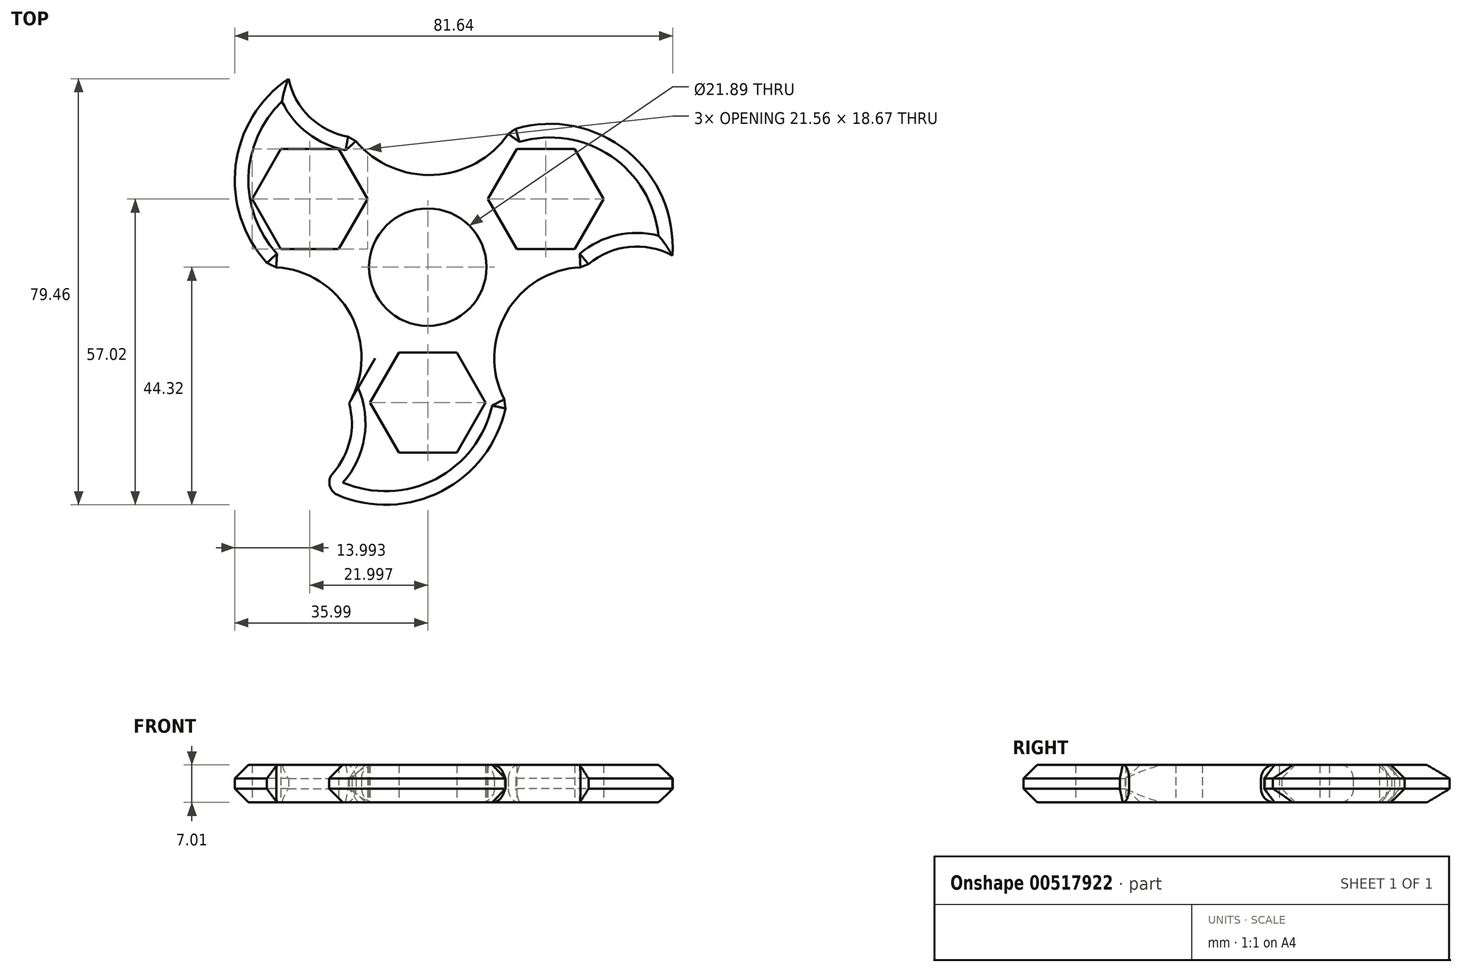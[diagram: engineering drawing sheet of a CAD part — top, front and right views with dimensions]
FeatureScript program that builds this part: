
annotation { "Feature Type Name" : "Feature", "Feature Type Description" : "" }
export const myFeature = defineFeature(function(context is Context, id is Id, definition is map)
    precondition{}
    {
        {
            var Q0;
            Q0=qCreatedBy(makeId("Top.planeOp"),FACE);
            var sketch = newSketch(context, id + "F0", { "sketchPlane" : qUnion([Q0])});
            skCircle(sketch, "E0.cCircle", {"center": v(0, 0) * mm, "radius": 12.7 * mm, "construction": true});
            skLineSegment(sketch, "E0.0", {"start": v(7.33, -12.7) * mm, "end": v(-7.33, -12.7) * mm});
            skLineSegment(sketch, "E0.1", {"start": v(-7.33, -12.7) * mm, "end": v(-14.66, 0) * mm});
            skLineSegment(sketch, "E0.2", {"start": v(-14.66, 0) * mm, "end": v(-7.33, 12.7) * mm});
            skLineSegment(sketch, "E0.4", {"start": v(7.33, 12.7) * mm, "end": v(14.66, 0) * mm});
            skLineSegment(sketch, "E0.5", {"start": v(14.66, 0) * mm, "end": v(7.33, -12.7) * mm});
            skCircle(sketch, "E1", {"center": v(0, 0) * mm, "radius": 10.95 * mm});
            skLineSegment(sketch, "E2.bottom", {"start": v(4.8, -12.7) * mm, "end": v(-4.8, -12.7) * mm});
            skLineSegment(sketch, "E3.MirrorCS", {"start": v(4.8, -76.2) * mm, "end": v(-4.8, -76.2) * mm});
            skLineSegment(sketch, "E4.MirrorCS", {"start": v(4.8, -73.66) * mm, "end": v(4.8, -76.2) * mm});
            skLineSegment(sketch, "E5.MirrorCS", {"start": v(14.66, -25.4) * mm, "end": v(7.33, -12.7) * mm});
            skLineSegment(sketch, "E6.MirrorCS", {"start": v(-7.33, -12.7) * mm, "end": v(-14.66, -25.4) * mm});
            skLineSegment(sketch, "E7", {"start": v(-7.33, 12.7) * mm, "end": v(7.33, 12.7) * mm});
            skLineSegment(sketch, "E8", {"start": v(0, 0) * mm, "end": v(0, -38.1) * mm});
            skPoint(sketch, "E8.endSnap0", {"position": v(0, -25.56) * mm});
            skLineSegment(sketch, "E9", {"start": v(0, -38.1) * mm, "end": v(0, 0) * mm});
            skLineSegment(sketch, "E10", {"start": v(0, 0) * mm, "end": v(44, 25.4) * mm});
            skLineSegment(sketch, "E11", {"start": v(44, 25.4) * mm, "end": v(0, 0) * mm});
            skLineSegment(sketch, "E12", {"start": v(0, 0) * mm, "end": v(-33, 19.05) * mm});
            skLineSegment(sketch, "E13.0", {"start": v(-7.33, 12.7) * mm, "end": v(-14.66, 0) * mm});
            skLineSegment(sketch, "E13.1", {"start": v(-14.66, 0) * mm, "end": v(-29.23, 0) * mm});
            skLineSegment(sketch, "E13.5", {"start": v(-13.97, 24.19) * mm, "end": v(-7.33, 12.7) * mm});
            skPoint(sketch, "E13.0.midPoint", {"position": v(-11, 6.35) * mm});
            skLineSegment(sketch, "E14.0", {"start": v(14.66, 0) * mm, "end": v(7.33, 12.7) * mm});
            skLineSegment(sketch, "E14.1", {"start": v(7.33, 12.7) * mm, "end": v(15.48, 25.53) * mm});
            skLineSegment(sketch, "E14.5", {"start": v(29.33, 0) * mm, "end": v(14.66, 0) * mm});
            skPoint(sketch, "E14.0.midPoint", {"position": v(11, 6.35) * mm});
            skArc(sketch, "E15", {"start": v(-14.66, -25.4) * mm, "mid": v(-14.6, -8.48) * mm, "end": v(-29.23, 0) * mm});
            skArc(sketch, "E16", {"start": v(29.33, 0) * mm, "mid": v(14.66, -8.47) * mm, "end": v(14.66, -25.4) * mm});
            skLineSegment(sketch, "E17.0", {"start": v(-7.33, -12.7) * mm, "end": v(7.33, -12.7) * mm});
            skLineSegment(sketch, "E17.1", {"start": v(7.33, -12.7) * mm, "end": v(14.66, -25.4) * mm});
            skLineSegment(sketch, "E17.5", {"start": v(-14.66, -25.4) * mm, "end": v(-7.33, -12.7) * mm});
            skPoint(sketch, "E17.0.midPoint", {"position": v(0, -12.7) * mm});
            skCircle(sketch, "E18.cCircle", {"center": v(-22, 12.7) * mm, "radius": 9.33 * mm, "construction": true});
            skLineSegment(sketch, "E18.0", {"start": v(-11.22, 12.7) * mm, "end": v(-16.6, 3.37) * mm});
            skLineSegment(sketch, "E18.1", {"start": v(-16.6, 3.37) * mm, "end": v(-27.39, 3.37) * mm});
            skLineSegment(sketch, "E18.2", {"start": v(-27.39, 3.37) * mm, "end": v(-32.78, 12.7) * mm});
            skLineSegment(sketch, "E18.3", {"start": v(-32.78, 12.7) * mm, "end": v(-27.39, 22.03) * mm});
            skLineSegment(sketch, "E18.4", {"start": v(-27.39, 22.03) * mm, "end": v(-16.6, 22.03) * mm});
            skLineSegment(sketch, "E18.5", {"start": v(-16.6, 22.03) * mm, "end": v(-11.22, 12.7) * mm});
            skPoint(sketch, "E18.0.midPoint", {"position": v(-13.91, 8.03) * mm});
            skCircle(sketch, "E19.cCircle", {"center": v(22, 12.7) * mm, "radius": 9.33 * mm, "construction": true});
            skLineSegment(sketch, "E19.0", {"start": v(16.6, 3.37) * mm, "end": v(11.22, 12.7) * mm});
            skLineSegment(sketch, "E19.1", {"start": v(11.22, 12.7) * mm, "end": v(16.6, 22.03) * mm});
            skLineSegment(sketch, "E19.2", {"start": v(16.6, 22.03) * mm, "end": v(27.39, 22.03) * mm});
            skLineSegment(sketch, "E19.3", {"start": v(27.39, 22.03) * mm, "end": v(32.78, 12.7) * mm});
            skLineSegment(sketch, "E19.4", {"start": v(32.78, 12.7) * mm, "end": v(27.39, 3.37) * mm});
            skLineSegment(sketch, "E19.5", {"start": v(27.39, 3.37) * mm, "end": v(16.6, 3.37) * mm});
            skPoint(sketch, "E19.0.midPoint", {"position": v(13.91, 8.03) * mm});
            skCircle(sketch, "E20.cCircle", {"center": v(0, -25.26) * mm, "radius": 9.33 * mm, "construction": true});
            skLineSegment(sketch, "E20.0", {"start": v(-5.39, -15.93) * mm, "end": v(5.39, -15.93) * mm});
            skLineSegment(sketch, "E20.1", {"start": v(5.39, -15.93) * mm, "end": v(10.78, -25.26) * mm});
            skLineSegment(sketch, "E20.2", {"start": v(10.78, -25.26) * mm, "end": v(5.39, -34.6) * mm});
            skLineSegment(sketch, "E20.3", {"start": v(5.39, -34.6) * mm, "end": v(-5.39, -34.6) * mm});
            skLineSegment(sketch, "E20.4", {"start": v(-5.39, -34.6) * mm, "end": v(-10.78, -25.26) * mm});
            skLineSegment(sketch, "E20.5", {"start": v(-10.78, -25.26) * mm, "end": v(-5.39, -15.93) * mm});
            skPoint(sketch, "E20.0.midPoint", {"position": v(0, -15.93) * mm});
            skArc(sketch, "E21", {"start": v(-25.98, 35.14) * mm, "mid": v(-35.9, 18.34) * mm, "end": v(-29.23, 0) * mm});
            skArc(sketch, "E22", {"start": v(-20.24, -40.67) * mm, "mid": v(1.3, -42.4) * mm, "end": v(14.66, -25.4) * mm});
            skArc(sketch, "E23", {"start": v(-20.24, -40.67) * mm, "mid": v(-15, -33.93) * mm, "end": v(-14.66, -25.4) * mm});
            skArc(sketch, "E24", {"start": v(45.59, 2.18) * mm, "mid": v(36.8, 21.93) * mm, "end": v(15.48, 25.53) * mm});
            skArc(sketch, "E25", {"start": v(45.59, 2.18) * mm, "mid": v(37.1, 3.73) * mm, "end": v(29.33, 0) * mm});
            skArc(sketch, "E26", {"start": v(-25.98, 35.14) * mm, "mid": v(-21.73, 27.74) * mm, "end": v(-13.97, 24.19) * mm});
            skArc(sketch, "E27", {"start": v(-13.97, 24.19) * mm, "mid": v(1.1, 17.2) * mm, "end": v(15.48, 25.53) * mm});
            skSolve(sketch);
        }
        {
            var Q0;
            Q0 = qSketchRegion(id + "F0", true);
            var Q1;
            {var subQ5=sQuery(id+"F0.wireOp",EDGE,"E7");Q1=makeQuery(id+"F0.imprint","IMPRINT",FACE,{"disambiguationData":[TD([[makeQuery(id+"F0.imprint","IMPRINT",EDGE,{"derivedFrom":subQ5}),-1.0]])]});}
            var Q2;
            {var subQ5=sQuery(id+"F0.wireOp",EDGE,"E0.5");Q2=makeQuery(id+"F0.imprint","IMPRINT",FACE,{"disambiguationData":[TD([[makeQuery(id+"F0.imprint","IMPRINT",EDGE,{"derivedFrom":subQ5}),-1.0]])]});}
            var Q3;
            {var subQ6=sQuery(id+"F0.wireOp",EDGE,"E0.1");Q3=makeQuery(id+"F0.imprint","IMPRINT",FACE,{"disambiguationData":[TD([[makeQuery(id+"F0.imprint","IMPRINT",EDGE,{"derivedFrom":subQ6}),-1.0]])]});}
            extrude(context, id + "F1", {"entities" : qUnion([Q0, Q1, Q2, Q3]), "depth" : 7 * mm, "offsetDistance" : 25.4 * mm});
        }
        {
            var Q0;
            Q0=makeQuery(id+"F1.opExtrude","CAP_EDGE",EDGE,{"disambiguationData":[OSD([sQuery(id+"F0.wireOp",EDGE,"E27")])],"isStart":false});
            var Q1;
            Q1=makeQuery(id+"F1.opExtrude","CAP_EDGE",EDGE,{"disambiguationData":[OSD([sQuery(id+"F0.wireOp",EDGE,"E27")])],"isStart":true});
            var Q2;
            Q2=makeQuery(id+"F1.opExtrude","CAP_EDGE",EDGE,{"disambiguationData":[OSD([sQuery(id+"F0.wireOp",EDGE,"E15")])],"isStart":true});
            var Q3;
            Q3=makeQuery(id+"F1.opExtrude","CAP_EDGE",EDGE,{"disambiguationData":[OSD([sQuery(id+"F0.wireOp",EDGE,"E15")])],"isStart":false});
            var Q4;
            Q4=makeQuery(id+"F1.opExtrude","CAP_EDGE",EDGE,{"disambiguationData":[OSD([sQuery(id+"F0.wireOp",EDGE,"E16")])],"isStart":true});
            var Q5;
            Q5=makeQuery(id+"F1.opExtrude","CAP_EDGE",EDGE,{"disambiguationData":[OSD([sQuery(id+"F0.wireOp",EDGE,"E16")])],"isStart":false});
            var Q6;
            Q6=makeQuery(id+"F1.opExtrude","SWEPT_EDGE",EDGE,{"disambiguationData":[OSD([sQuery(id+"F0.wireOp",EDGE,"E17.5"),sQuery(id+"F0.wireOp",EDGE,"E23")])]});
            fillet(context, id + "F2", {"entities" : qUnion([Q0, Q1, Q2, Q3, Q4, Q5, Q6]), "radius" : 2.54 * mm, "tangentPropagation" : true, "allowEdgeOverflow" : false});
        }
        {
            var Q0;
            Q0=makeQuery(id+"F1.opExtrude","CAP_EDGE",EDGE,{"disambiguationData":[OSD([sQuery(id+"F0.wireOp",EDGE,"E22")])],"isStart":false});
            var Q1;
            Q1=makeQuery(id+"F1.opExtrude","CAP_EDGE",EDGE,{"disambiguationData":[OSD([sQuery(id+"F0.wireOp",EDGE,"E22")])],"isStart":true});
            var Q2;
            Q2=makeQuery(id+"F1.opExtrude","CAP_EDGE",EDGE,{"disambiguationData":[OSD([sQuery(id+"F0.wireOp",EDGE,"E23")])],"isStart":false});
            var Q3;
            Q3=makeQuery(id+"F1.opExtrude","CAP_EDGE",EDGE,{"disambiguationData":[OSD([sQuery(id+"F0.wireOp",EDGE,"E23")])],"isStart":true});
            var Q4;
            Q4=makeQuery(id+"F1.opExtrude","CAP_EDGE",EDGE,{"disambiguationData":[OSD([sQuery(id+"F0.wireOp",EDGE,"E21")])],"isStart":true});
            var Q5;
            Q5=makeQuery(id+"F1.opExtrude","CAP_EDGE",EDGE,{"disambiguationData":[OSD([sQuery(id+"F0.wireOp",EDGE,"E21")])],"isStart":false});
            var Q6;
            Q6=makeQuery(id+"F1.opExtrude","CAP_EDGE",EDGE,{"disambiguationData":[OSD([sQuery(id+"F0.wireOp",EDGE,"E26")])],"isStart":true});
            var Q7;
            Q7=makeQuery(id+"F1.opExtrude","CAP_EDGE",EDGE,{"disambiguationData":[OSD([sQuery(id+"F0.wireOp",EDGE,"E24")])],"isStart":false});
            var Q8;
            Q8=makeQuery(id+"F1.opExtrude","CAP_EDGE",EDGE,{"disambiguationData":[OSD([sQuery(id+"F0.wireOp",EDGE,"E25")])],"isStart":false});
            var Q9;
            Q9=makeQuery(id+"F1.opExtrude","CAP_EDGE",EDGE,{"disambiguationData":[OSD([sQuery(id+"F0.wireOp",EDGE,"E25")])],"isStart":true});
            chamfer(context, id + "F3", {"entities" : qUnion([Q0, Q1, Q2, Q3, Q4, Q5, Q6, Q7, Q8, Q9]), "width" : 2.54 * mm, "tangentPropagation" : true});
        }
    });
